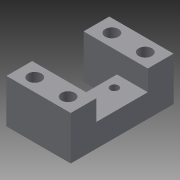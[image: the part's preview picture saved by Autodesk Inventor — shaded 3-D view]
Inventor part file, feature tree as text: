
AUTODESK INVENTOR PART (.ipt)
format: ipt  version: 2015 (Build 190159000, 159)  size: 117,248 bytes
history: native  units: in
note: dims shown in document units (in); Inventor stores cm internally (conversion verified against a paired STEP export)
features: extrude x2, sketch x1
ambient origin geometry x8: Origin, YZ Plane, XZ Plane, XY Plane, X Axis, Y Axis, Z Axis, Center Point
bodies: Solid1 (feature_tree)
feature tree (3):
  sketch  "Sketch1"  dims[d0=0.3937in d1=0.3937in d2=0.5118in d3=0.3937in d4=0.9843in d5=0.5118in d6=0.3937in d7=0.9843in d8=0.2362in d9=0.2362in d10=0.2362in d11=0.2362in d12=0.2047in d13=0.2047in d14=0.2047in d15=0.2047in d16=0.1575in d17=0.1969in d18=0.1969in d19=0.126in d20=0.126in d21=0.6693in d22=0.0in d23=0.3543in d24=0.0in]
  extrude  "Extrusion1"  Depth=0.3937in
  extrude  "Extrusion2"  Depth=0.5118in
